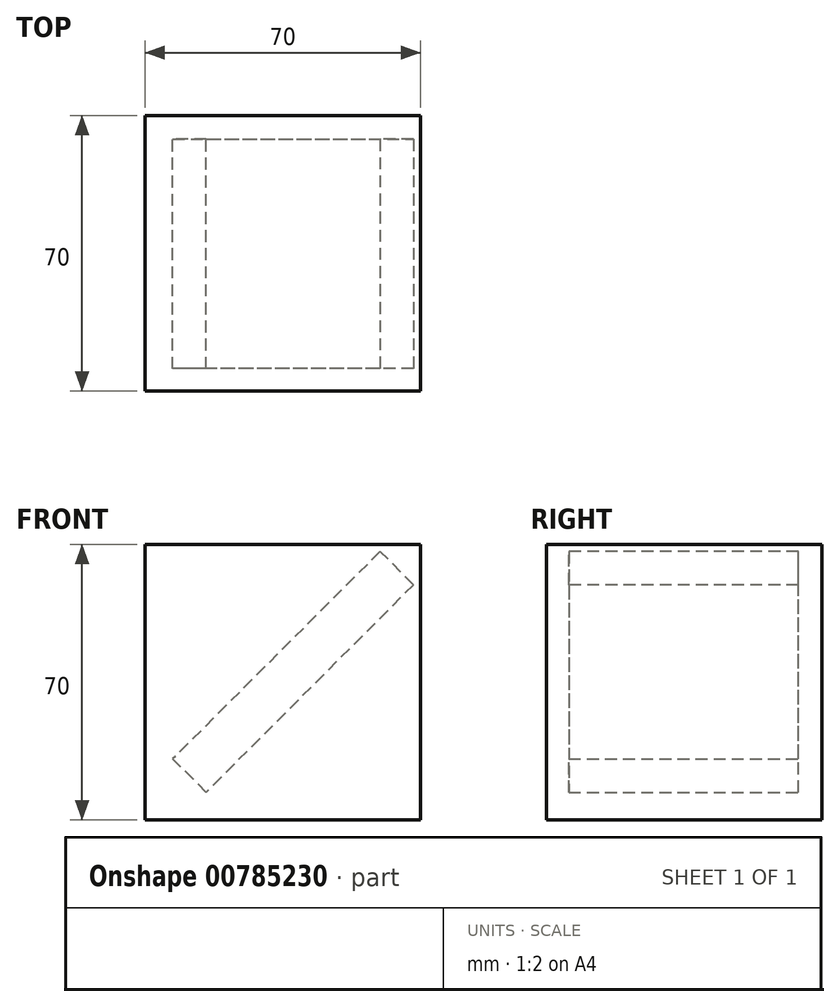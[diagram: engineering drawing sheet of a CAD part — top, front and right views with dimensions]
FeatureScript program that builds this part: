
annotation { "Feature Type Name" : "Feature", "Feature Type Description" : "" }
export const myFeature = defineFeature(function(context is Context, id is Id, definition is map)
    precondition{}
    {
        {
            var Q0;
            Q0=qCreatedBy(makeId("Top.planeOp"),FACE);
            var sketch = newSketch(context, id + "F0", { "sketchPlane" : qUnion([Q0])});
            skSolve(sketch);
        }
        {
            var Q0;
            Q0=qCreatedBy(makeId("Top.planeOp"),FACE);
            var sketch = newSketch(context, id + "F1", { "sketchPlane" : qUnion([Q0])});
            skCircle(sketch, "E0", {"center": v(-43.89, -28.76) * mm, "radius": 90.44 * mm, "construction": true});
            skLineSegment(sketch, "E1", {"start": v(18.4, -28.76) * mm, "end": v(-43.89, 33.54) * mm});
            skCircle(sketch, "E2", {"center": v(-43.89, 33.54) * mm, "radius": 88.1 * mm, "construction": true});
            skLineSegment(sketch, "E3", {"start": v(-43.89, 33.54) * mm, "end": v(44.2, 33.54) * mm, "construction": true});
            skLineSegment(sketch, "E4", {"start": v(-43.89, 33.54) * mm, "end": v(-43.89, -28.76) * mm});
            skLineSegment(sketch, "E5", {"start": v(-43.89, -28.76) * mm, "end": v(18.4, -28.76) * mm});
            skLineSegment(sketch, "E6", {"start": v(44.2, 33.54) * mm, "end": v(44.2, -84.29) * mm});
            skLineSegment(sketch, "E7", {"start": v(0.16, 109.83) * mm, "end": v(0.16, -42.76) * mm});
            skLineSegment(sketch, "E8", {"start": v(-43.89, -28.76) * mm, "end": v(46.56, -28.76) * mm});
            skLineSegment(sketch, "E9", {"start": v(-43.89, 33.54) * mm, "end": v(-43.89, 33.54) * mm});
            skArc(sketch, "E10", {"start": v(-43.89, 33.54) * mm, "mid": v(-87.94, -72.8) * mm, "end": v(18.4, -28.76) * mm, "construction": true});
            skArc(sketch, "E11", {"start": v(18.4, -28.76) * mm, "mid": v(0.16, 15.3) * mm, "end": v(-43.89, 33.54) * mm});
            skLineSegment(sketch, "E12", {"start": v(-43.89, -28.76) * mm, "end": v(-12.74, 2.4) * mm});
            skLineSegment(sketch, "E13", {"start": v(-12.74, 2.4) * mm, "end": v(90.44, 105.57) * mm});
            skLineSegment(sketch, "E14", {"start": v(20.07, 35.2) * mm, "end": v(20.07, -28.76) * mm});
            skLineSegment(sketch, "E15", {"start": v(20.07, 35.2) * mm, "end": v(-43.89, 35.2) * mm});
            skLineSegment(sketch, "E16", {"start": v(-43.89, 35.2) * mm, "end": v(-43.89, 33.54) * mm});
            skLineSegment(sketch, "E17.bottom", {"start": v(-43.89, 35.2) * mm, "end": v(20.07, 35.2) * mm});
            skLineSegment(sketch, "E17.top", {"start": v(-43.89, -28.76) * mm, "end": v(20.07, -28.76) * mm});
            skLineSegment(sketch, "E17.left", {"start": v(-43.89, 35.2) * mm, "end": v(-43.89, -28.76) * mm});
            skSolve(sketch);
        }
        {
            var Q0;
            Q0=qCreatedBy(makeId("Top.planeOp"),FACE);
            var sketch = newSketch(context, id + "F2", { "sketchPlane" : qUnion([Q0])});
            skLineSegment(sketch, "E18.0", {"start": v(-43.89, 35.2) * mm, "end": v(20.07, 35.2) * mm});
            skLineSegment(sketch, "E19.0", {"start": v(-43.89, 35.2) * mm, "end": v(-43.89, -28.76) * mm});
            skLineSegment(sketch, "E20.0", {"start": v(20.07, 35.2) * mm, "end": v(20.07, -28.76) * mm});
            skLineSegment(sketch, "E21.top", {"start": v(-43.89, -28.76) * mm, "end": v(20.07, -28.76) * mm});
            skSolve(sketch);
        }
        {
            var Q0;
            Q0=makeQuery(id+"F2.imprint","IMPRINT",FACE,{"disambiguationData":[TD([[makeQuery(id+"F2.imprint","IMPRINT",EDGE,{"derivedFrom":sQuery(id+"F2.wireOp",EDGE,"E18.0")}),-1.0]])]});
            extrude(context, id + "F3", {"entities" : qUnion([Q0]), "depth" : 64 * mm, "offsetDistance" : 25 * mm});
        }
        {
            var Q0;
            Q0=makeQuery(id+"F3.opExtrude","SWEPT_FACE",FACE,{"disambiguationData":[OSD([sQuery(id+"F2.wireOp",EDGE,"E18.0")])]});
            var sketch = newSketch(context, id + "F4", { "sketchPlane" : qUnion([Q0])});
            skLineSegment(sketch, "E22", {"start": v(43.89, 0) * mm, "end": v(-20.07, 64) * mm});
            skSolve(sketch);
        }
        {
            var Q0;
            Q0=sQuery(id+"F4.wireOp",EDGE,"E22");
            extrude(context, id + "F5", {"bodyType" : ToolBodyType.SURFACE, "surfaceEntities" : qUnion([Q0]), "oppositeDirection" : true, "depth" : 107.2 * mm, "offsetDistance" : 25 * mm});
        }
        {
            var Q0;
            Q0=makeQuery(id+"F5.opExtrude","SWEPT_FACE",FACE,{"disambiguationData":[OSD([sQuery(id+"F4.wireOp",EDGE,"E22")])]});
            var sketch = newSketch(context, id + "F6", { "sketchPlane" : qUnion([Q0])});
            skLineSegment(sketch, "E23", {"start": v(35.2, -31.02) * mm, "end": v(-28.76, -31.02) * mm});
            skLineSegment(sketch, "E24", {"start": v(-28.76, -31.02) * mm, "end": v(-28.76, 59.45) * mm});
            skLineSegment(sketch, "E25", {"start": v(-23.09, 59.45) * mm, "end": v(-23.09, -15.06) * mm});
            skLineSegment(sketch, "E26", {"start": v(35.2, -15.06) * mm, "end": v(35.2, 59.45) * mm});
            skLineSegment(sketch, "E27", {"start": v(35.2, 59.45) * mm, "end": v(-23.09, 59.45) * mm});
            skLineSegment(sketch, "E28", {"start": v(-23.09, -15.06) * mm, "end": v(35.2, -15.06) * mm});
            skLineSegment(sketch, "E29.top", {"start": v(-23.09, 59.45) * mm, "end": v(35.2, 59.45) * mm});
            skLineSegment(sketch, "E29.left", {"start": v(-23.09, -15.06) * mm, "end": v(-23.09, 59.45) * mm});
            skSolve(sketch);
        }
        {
            var Q0;
            Q0=makeQuery(id+"F3.opExtrude","SWEPT_FACE",FACE,{"disambiguationData":[OSD([sQuery(id+"F2.wireOp",EDGE,"E21.top")])]});
            var sketch = newSketch(context, id + "F7", { "sketchPlane" : qUnion([Q0])});
            skLineSegment(sketch, "E30.bottom", {"start": v(-43.89, 0) * mm, "end": v(26.11, 0) * mm});
            skLineSegment(sketch, "E30.top", {"start": v(-43.89, 70) * mm, "end": v(26.11, 70) * mm});
            skLineSegment(sketch, "E30.left", {"start": v(-43.89, 0) * mm, "end": v(-43.89, 70) * mm});
            skLineSegment(sketch, "E30.right", {"start": v(26.11, 0) * mm, "end": v(26.11, 70) * mm});
            skSolve(sketch);
        }
        {
            var Q0;
            Q0 = qSketchRegion(id + "F7", true);
            extrude(context, id + "F8", {"entities" : qUnion([Q0]), "operationType" : NewBodyOperationType.ADD, "oppositeDirection" : true, "depth" : 70 * mm, "offsetDistance" : 25 * mm});
        }
        {
            var Q0;
            Q0 = qSketchRegion(id + "F6", true);
            extrude(context, id + "F9", {"entities" : qUnion([Q0]), "operationType" : NewBodyOperationType.ADD, "depth" : 5.7 * mm, "offsetDistance" : 25 * mm, "hasSecondDirection" : true, "secondDirectionOppositeDirection" : true, "secondDirectionDepth" : 6 * mm});
        }
        {
            var Q0;
            Q0=makeQuery(id+"F6.imprint","IMPRINT",FACE,{"disambiguationData":[TD([[makeQuery(id+"F6.imprint","IMPRINT",EDGE,{"derivedFrom":sQuery(id+"F6.wireOp",EDGE,"E28")}),1.0]])]});
            extrude(context, id + "F10", {"entities" : qUnion([Q0]), "depth" : 6 * mm, "offsetDistance" : 25 * mm, "hasSecondDirection" : true, "secondDirectionOppositeDirection" : true, "secondDirectionDepth" : 6 * mm});
        }
    });
